# Revit family: KJU-ECMD-DAFWSxxx
name_source: partatom
category: Leuchten
units: mm (PartAtom-declared; Revit-internal decimal feet)

## family parameters
Basisbauteil = Fläche
Beim Laden mit Abzugskörper schneiden = Nein
Bemaßung runder Anschluss = Durchmesser verwenden
Gemeinsam genutzt = Nein
Lichtquelle = Ja
OmniClass-Nummer = 23.80.70.11
OmniClass-Titel = Luminaries for Internal Lighting
Raumberechnungspunkt = Nein
Teiletyp = Normal

## types (6) — shared parameters
Baugruppenkennzeichen = D5020200
Emissionsform beim Rendern sichtbar = Nein
Farbfilter = 16777215
Farbtemperaturverschiebung bei Dämpfen der Lampe = <Keine Auswahl>
Hersteller = RIDI Leuchten GmbH
Lampe = LED
Neigungswinkel = 90.00°
URL = www.spectral.de
Von Kreisdurchmesser aussenden = 280 mm  [stored 0.918635 ft]
brand = Spectral
conformity mark = CE
electrical safety class = 1
height = 90 mm  [stored 0.295276 ft]
ingress protection (IP) code = IP20
length = 354 mm  [stored 1.16142 ft]
nominal frequency = 50-60Hz
nominal voltage = 230
voltage type (AC, DC, UC) = AC
weight = 2,9kg
width = 354 mm  [stored 1.16142 ft]
zero-valued in all types: Vorgabe-Ansicht

## per-type parameters (varying)
| type | Datei für fotometrisches Netz | Modell | Scheinlast | rated input power |
| KJU-ECMD DAFWS830APS0125 | KJU-xCD xxxAPSxx.IES | SPG0830006AH | 11 VA | 11 |
| KJU-ECMD DAFWS830APS0250 | KJU-xCD xxxAPSxx.IES | SPG0830007AH | 25 VA | 25 |
| KJU-ECMD DAFWS830OS0300 | KJU-xCD xxxOSxx.IES | SPG0830031AH | 25 VA | 25 |
| KJU-ECMD DAFWS840APS0125 | KJU-xCD xxxAPSxx.IES | SPG0830009AH | 11 VA | 11 |
| KJU-ECMD DAFWS840APS0300 | KJU-xCD xxxAPSxx.IES | SPG0830010AH | 25 VA | 25 |
| KJU-ECMD DAFWS840OS0350 | KJU-xCD xxxOSxx.IES | SPG0830011AH | 25 VA | 25 |

note: column(s) folded — value = type name in every type: product name

note: [stored X ft] marks values corroborated as IEEE doubles in the binary element streams (Revit-internal decimal feet)
